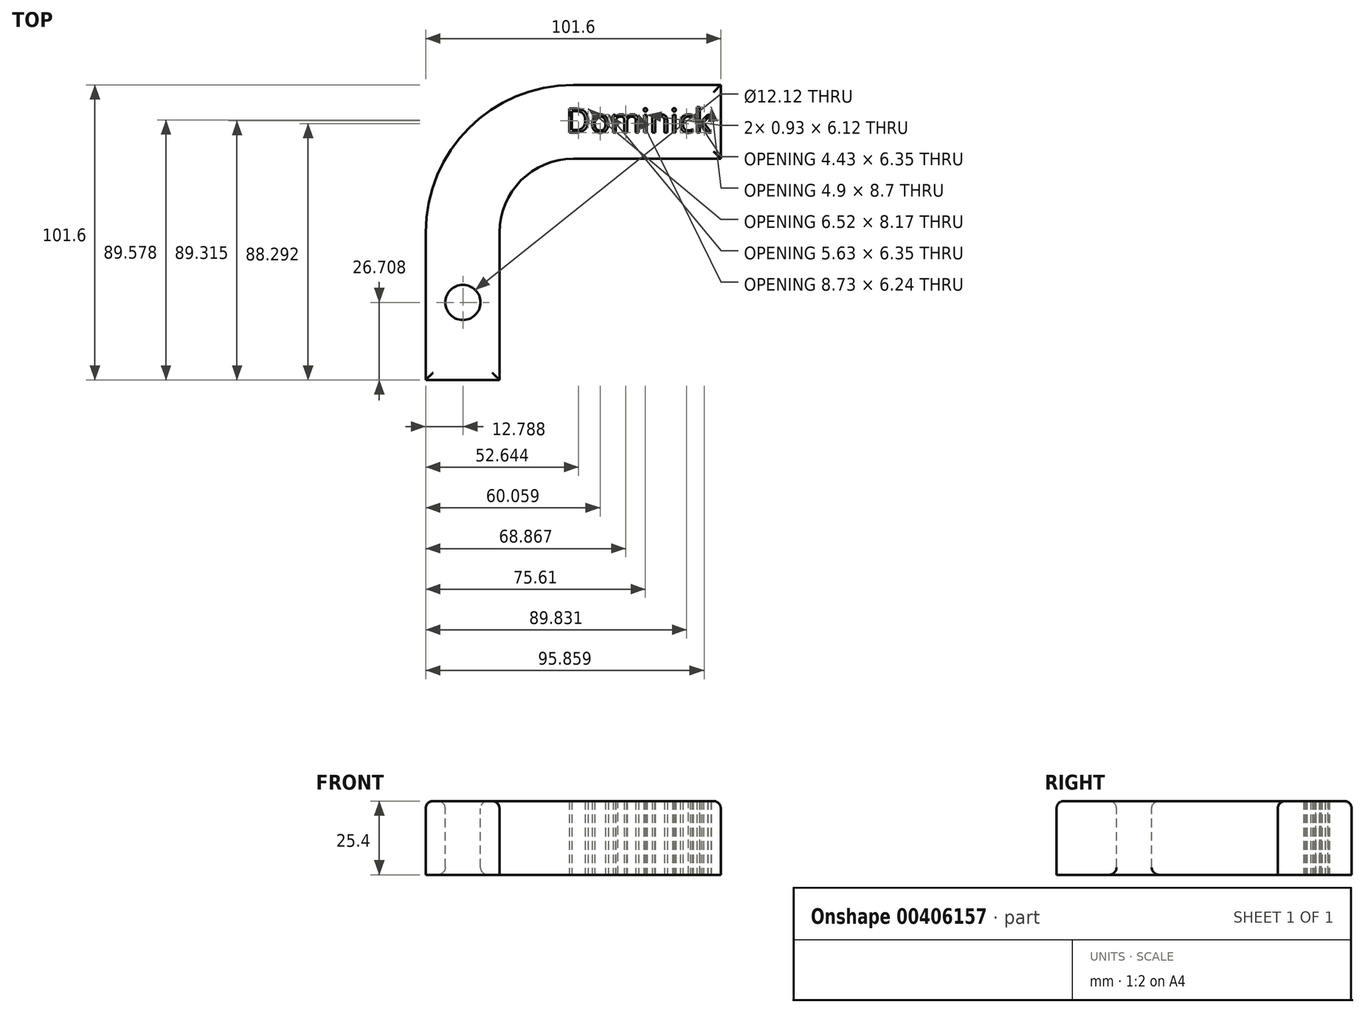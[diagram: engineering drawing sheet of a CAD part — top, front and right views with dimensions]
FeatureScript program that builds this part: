
annotation { "Feature Type Name" : "Feature", "Feature Type Description" : "" }
export const myFeature = defineFeature(function(context is Context, id is Id, definition is map)
    precondition{}
    {
        {
            var Q0;
            Q0=qCreatedBy(makeId("Top.planeOp"),FACE);
            var sketch = newSketch(context, id + "F0", { "sketchPlane" : qUnion([Q0])});
            skLineSegment(sketch, "E0", {"start": v(-25.4, -50.8) * mm, "end": v(-50.8, -50.8) * mm});
            skLineSegment(sketch, "E1", {"start": v(-50.8, -50.8) * mm, "end": v(-50.8, 0) * mm});
            skLineSegment(sketch, "E2", {"start": v(-25.4, 0) * mm, "end": v(-25.4, -50.8) * mm});
            skLineSegment(sketch, "E3.MirrorCS", {"start": v(50.8, 25.4) * mm, "end": v(50.8, 50.8) * mm});
            skLineSegment(sketch, "E4.MirrorCS", {"start": v(0, 25.4) * mm, "end": v(50.8, 25.4) * mm});
            skLineSegment(sketch, "E5.MirrorCS", {"start": v(50.8, 50.8) * mm, "end": v(0, 50.8) * mm});
            skArc(sketch, "E6", {"start": v(0, 50.8) * mm, "mid": v(-35.92, 35.92) * mm, "end": v(-50.8, 0) * mm});
            skArc(sketch, "E7", {"start": v(0, 25.4) * mm, "mid": v(-17.96, 17.96) * mm, "end": v(-25.4, 0) * mm});
            skSolve(sketch);
        }
        {
            var Q0;
            Q0=qCreatedBy(makeId("Top.planeOp"),FACE);
            var sketch = newSketch(context, id + "F1", { "sketchPlane" : qUnion([Q0])});
            skText(sketch, "E8", { "text": "Dominick", "fontName": "OpenSans-Regular.ttf"});
            const initialGuessF1  = {"E8": [-0.00254, 0.03443, 1, 0, 0.00824]};
            skSetInitialGuess(sketch, initialGuessF1);
            skSolve(sketch);
        }
        {
            var Q0;
            Q0=makeQuery(id+"F0.imprint","IMPRINT",FACE,{"disambiguationData":[TD([[makeQuery(id+"F0.imprint","IMPRINT",EDGE,{"derivedFrom":sQuery(id+"F0.wireOp",EDGE,"E3.MirrorCS")}),1.0]])]});
            extrude(context, id + "F2", {"entities" : qUnion([Q0]), "depth" : 25.4 * mm});
        }
        {
            var Q0;
            Q0 = qSketchRegion(id + "F1", true);
            extrude(context, id + "F3", {"entities" : qUnion([Q0]), "operationType" : NewBodyOperationType.REMOVE, "depth" : 25.4 * mm});
        }
        {
            var Q0;
            Q0=makeQuery(id+"F2.opExtrude","CAP_EDGE",EDGE,{"disambiguationData":[OSD([sQuery(id+"F0.wireOp",EDGE,"E4.MirrorCS")])],"isStart":false});
            var Q1;
            Q1=makeQuery(id+"F2.opExtrude","CAP_EDGE",EDGE,{"disambiguationData":[OSD([sQuery(id+"F0.wireOp",EDGE,"E5.MirrorCS")])],"isStart":false});
            var Q2;
            Q2=makeQuery(id+"F2.opExtrude","CAP_EDGE",EDGE,{"disambiguationData":[OSD([sQuery(id+"F0.wireOp",EDGE,"E3.MirrorCS")])],"isStart":false});
            var Q3;
            Q3=makeQuery(id+"F2.opExtrude","CAP_EDGE",EDGE,{"disambiguationData":[OSD([sQuery(id+"F0.wireOp",EDGE,"E0")])],"isStart":false});
            fillet(context, id + "F4", {"entities" : qUnion([Q0, Q1, Q2, Q3]), "radius" : 2.54 * mm, "tangentPropagation" : true, "allowEdgeOverflow" : false});
        }
        {
            var Q0;
            {var subQ0=sQuery(id+"F0.wireOp",EDGE,"E5.MirrorCS");var subQ1=sQuery(id+"F0.wireOp",EDGE,"E4.MirrorCS");var subQ2=sQuery(id+"F0.wireOp",EDGE,"E0");var subQ3=sQuery(id+"F0.wireOp",EDGE,"E3.MirrorCS");var subQ4=sQuery(id+"F0.wireOp",EDGE,"E1");var subQ5=sQuery(id+"F0.wireOp",EDGE,"E6");var subQ6=sQuery(id+"F0.wireOp",EDGE,"E2");var subQ7=sQuery(id+"F0.wireOp",EDGE,"E7");Q0=makeQuery(id+"F3.boolean.opBoolean","SPLIT",FACE,{"disambiguationData":[TD([makeQuery(id+"F2.opExtrude","SWEPT_FACE",FACE,{"disambiguationData":[OSD([subQ3])]})])],"derivedFrom":makeQuery(id+"F2.opExtrude","CAP_FACE",FACE,{"disambiguationData":[OSD([subQ3,subQ1,subQ0,subQ2,subQ6,subQ4,subQ5,subQ7])],"isStart":false})});}
            var sketch = newSketch(context, id + "F5", { "sketchPlane" : qUnion([Q0])});
            skCircle(sketch, "E9", {"center": v(-38.01, -24.1) * mm, "radius": 6.06 * mm});
            skSolve(sketch);
        }
        {
            var Q0;
            Q0 = qSketchRegion(id + "F5", true);
            extrude(context, id + "F6", {"entities" : qUnion([Q0]), "operationType" : NewBodyOperationType.REMOVE, "oppositeDirection" : true, "depth" : 25.4 * mm});
        }
        {
            var Q0;
            Q0=makeQuery(id+"F6.boolean.opBoolean","COPY",FACE,{"derivedFrom":makeQuery(id+"F6.opExtrude","SWEPT_FACE",FACE,{"disambiguationData":[OSD([sQuery(id+"F5.wireOp",EDGE,"E9")])]})});
            fillet(context, id + "F7", {"entities" : qUnion([Q0]), "radius" : 2.54 * mm, "tangentPropagation" : true, "allowEdgeOverflow" : false});
        }
    });
